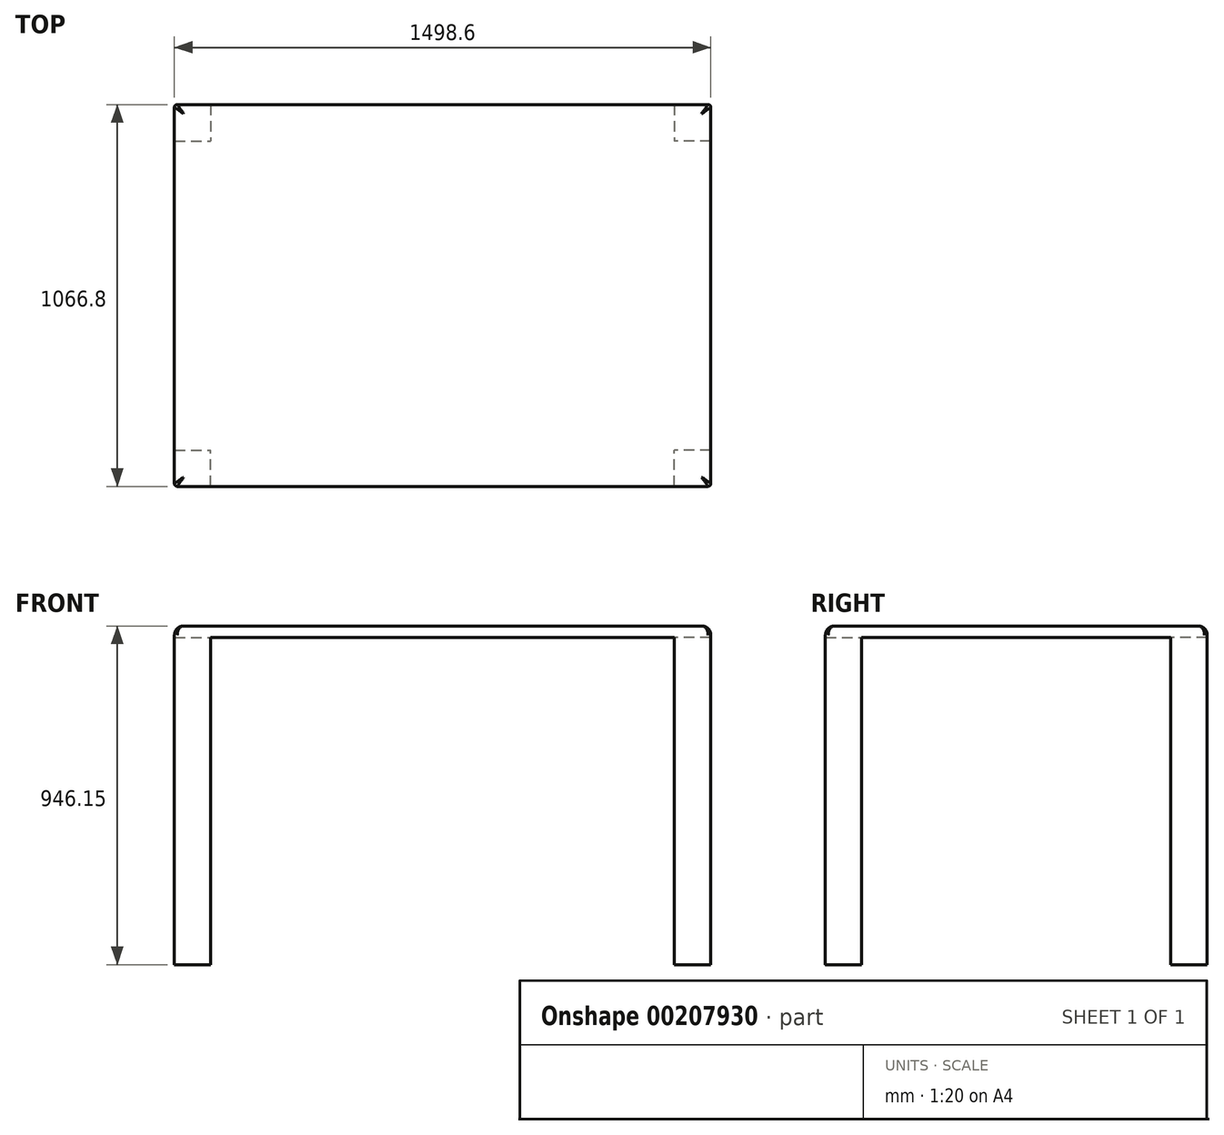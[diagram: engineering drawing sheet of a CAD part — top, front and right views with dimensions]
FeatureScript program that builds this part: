
annotation { "Feature Type Name" : "Feature", "Feature Type Description" : "" }
export const myFeature = defineFeature(function(context is Context, id is Id, definition is map)
    precondition{}
    {
        {
            var Q0;
            Q0=qCreatedBy(makeId("Top.planeOp"),FACE);
            var sketch = newSketch(context, id + "F0", { "sketchPlane" : qUnion([Q0])});
            skLineSegment(sketch, "E0.bottom", {"start": v(-749.3, 533.4) * mm, "end": v(749.3, 533.4) * mm});
            skLineSegment(sketch, "E0.top", {"start": v(-749.3, -533.4) * mm, "end": v(749.3, -533.4) * mm});
            skLineSegment(sketch, "E0.left", {"start": v(-749.3, 533.4) * mm, "end": v(-749.3, -533.4) * mm});
            skLineSegment(sketch, "E0.right", {"start": v(749.3, 533.4) * mm, "end": v(749.3, -533.4) * mm});
            skSolve(sketch);
        }
        {
            var Q0;
            Q0=makeQuery(id+"F0.imprint","IMPRINT",FACE,{"disambiguationData":[TD([[makeQuery(id+"F0.imprint","IMPRINT",EDGE,{"derivedFrom":sQuery(id+"F0.wireOp",EDGE,"E0.bottom")}),-1.0]])]});
            extrude(context, id + "F1", {"entities" : qUnion([Q0]), "depth" : 31.75 * mm});
        }
        {
            var Q0;
            Q0=makeQuery(id+"F1.opExtrude","CAP_EDGE",EDGE,{"disambiguationData":[OSD([sQuery(id+"F0.wireOp",EDGE,"E0.bottom")])],"isStart":false});
            var Q1;
            Q1=makeQuery(id+"F1.opExtrude","CAP_EDGE",EDGE,{"disambiguationData":[OSD([sQuery(id+"F0.wireOp",EDGE,"E0.left")])],"isStart":false});
            var Q2;
            Q2=makeQuery(id+"F1.opExtrude","CAP_EDGE",EDGE,{"disambiguationData":[OSD([sQuery(id+"F0.wireOp",EDGE,"E0.top")])],"isStart":false});
            var Q3;
            Q3=makeQuery(id+"F1.opExtrude","CAP_EDGE",EDGE,{"disambiguationData":[OSD([sQuery(id+"F0.wireOp",EDGE,"E0.right")])],"isStart":false});
            fillet(context, id + "F2", {"entities" : qUnion([Q0, Q1, Q2, Q3]), "radius" : 25.4 * mm, "tangentPropagation" : true, "allowEdgeOverflow" : false});
        }
        {
            var Q0;
            Q0=makeQuery(id+"F1.opExtrude","CAP_FACE",FACE,{"disambiguationData":[OSD([sQuery(id+"F0.wireOp",EDGE,"E0.bottom"),sQuery(id+"F0.wireOp",EDGE,"E0.top"),sQuery(id+"F0.wireOp",EDGE,"E0.left"),sQuery(id+"F0.wireOp",EDGE,"E0.right")])],"isStart":true});
            var sketch = newSketch(context, id + "F3", { "sketchPlane" : qUnion([Q0])});
            skLineSegment(sketch, "E1.bottom", {"start": v(-749.3, 533.4) * mm, "end": v(-647.7, 533.4) * mm});
            skLineSegment(sketch, "E1.top", {"start": v(-749.3, 431.8) * mm, "end": v(-647.7, 431.8) * mm});
            skLineSegment(sketch, "E1.left", {"start": v(-749.3, 533.4) * mm, "end": v(-749.3, 431.8) * mm});
            skLineSegment(sketch, "E1.right", {"start": v(-647.7, 533.4) * mm, "end": v(-647.7, 431.8) * mm});
            skLineSegment(sketch, "E2.bottom", {"start": v(749.3, 533.4) * mm, "end": v(647.7, 533.4) * mm});
            skLineSegment(sketch, "E2.top", {"start": v(749.3, 431.8) * mm, "end": v(647.7, 431.8) * mm});
            skLineSegment(sketch, "E2.left", {"start": v(749.3, 533.4) * mm, "end": v(749.3, 431.8) * mm});
            skLineSegment(sketch, "E2.right", {"start": v(647.7, 533.4) * mm, "end": v(647.7, 431.8) * mm});
            skLineSegment(sketch, "E3.bottom", {"start": v(-749.3, -533.4) * mm, "end": v(-647.7, -533.4) * mm});
            skLineSegment(sketch, "E3.top", {"start": v(-749.3, -431.8) * mm, "end": v(-647.7, -431.8) * mm});
            skLineSegment(sketch, "E3.left", {"start": v(-749.3, -533.4) * mm, "end": v(-749.3, -431.8) * mm});
            skLineSegment(sketch, "E3.right", {"start": v(-647.7, -533.4) * mm, "end": v(-647.7, -431.8) * mm});
            skLineSegment(sketch, "E4.bottom", {"start": v(749.3, -533.4) * mm, "end": v(647.7, -533.4) * mm});
            skLineSegment(sketch, "E4.top", {"start": v(749.3, -431.8) * mm, "end": v(647.7, -431.8) * mm});
            skLineSegment(sketch, "E4.left", {"start": v(749.3, -533.4) * mm, "end": v(749.3, -431.8) * mm});
            skLineSegment(sketch, "E4.right", {"start": v(647.7, -533.4) * mm, "end": v(647.7, -431.8) * mm});
            skSolve(sketch);
        }
        {
            var Q0;
            Q0=makeQuery(id+"F3.imprint","IMPRINT",FACE,{"disambiguationData":[TD([[makeQuery(id+"F3.imprint","IMPRINT",EDGE,{"derivedFrom":sQuery(id+"F3.wireOp",EDGE,"E2.bottom")}),-1.0]])]});
            var Q1;
            Q1=makeQuery(id+"F3.imprint","IMPRINT",FACE,{"disambiguationData":[TD([[makeQuery(id+"F3.imprint","IMPRINT",EDGE,{"derivedFrom":sQuery(id+"F3.wireOp",EDGE,"E3.bottom")}),1.0]])]});
            var Q2;
            Q2=makeQuery(id+"F3.imprint","IMPRINT",FACE,{"disambiguationData":[TD([[makeQuery(id+"F3.imprint","IMPRINT",EDGE,{"derivedFrom":sQuery(id+"F3.wireOp",EDGE,"E4.bottom")}),1.0]])]});
            var Q3;
            Q3=makeQuery(id+"F3.imprint","IMPRINT",FACE,{"disambiguationData":[TD([[makeQuery(id+"F3.imprint","IMPRINT",EDGE,{"derivedFrom":sQuery(id+"F3.wireOp",EDGE,"E1.bottom")}),-1.0]])]});
            extrude(context, id + "F4", {"entities" : qUnion([Q0, Q1, Q2, Q3]), "operationType" : NewBodyOperationType.ADD, "depth" : 914.4 * mm});
        }
        {
            var Q0;
            Q0=makeQuery(id+"F4.boolean.opBoolean","MERGE",EDGE,{"derivedFrom":[makeQuery(id+"F1.opExtrude","SWEPT_EDGE",EDGE,{"disambiguationData":[OSD([sQuery(id+"F0.wireOp",EDGE,"E0.bottom"),sQuery(id+"F0.wireOp",EDGE,"E0.left")])]}),makeQuery(id+"F4.opExtrude","SWEPT_EDGE",EDGE,{"disambiguationData":[OSD([sQuery(id+"F3.wireOp",EDGE,"E3.bottom"),sQuery(id+"F3.wireOp",EDGE,"E3.left")])]})]});
            var Q1;
            Q1=makeQuery(id+"F4.boolean.opBoolean","MERGE",EDGE,{"derivedFrom":[makeQuery(id+"F1.opExtrude","SWEPT_EDGE",EDGE,{"disambiguationData":[OSD([sQuery(id+"F0.wireOp",EDGE,"E0.bottom"),sQuery(id+"F0.wireOp",EDGE,"E0.right")])]}),makeQuery(id+"F4.opExtrude","SWEPT_EDGE",EDGE,{"disambiguationData":[OSD([sQuery(id+"F3.wireOp",EDGE,"E4.bottom"),sQuery(id+"F3.wireOp",EDGE,"E4.left")])]})]});
            var Q2;
            Q2=makeQuery(id+"F4.boolean.opBoolean","MERGE",EDGE,{"derivedFrom":[makeQuery(id+"F1.opExtrude","SWEPT_EDGE",EDGE,{"disambiguationData":[OSD([sQuery(id+"F0.wireOp",EDGE,"E0.top"),sQuery(id+"F0.wireOp",EDGE,"E0.left")])]}),makeQuery(id+"F4.opExtrude","SWEPT_EDGE",EDGE,{"disambiguationData":[OSD([sQuery(id+"F3.wireOp",EDGE,"E1.bottom"),sQuery(id+"F3.wireOp",EDGE,"E1.left")])]})]});
            var Q3;
            Q3=makeQuery(id+"F4.boolean.opBoolean","MERGE",EDGE,{"derivedFrom":[makeQuery(id+"F1.opExtrude","SWEPT_EDGE",EDGE,{"disambiguationData":[OSD([sQuery(id+"F0.wireOp",EDGE,"E0.top"),sQuery(id+"F0.wireOp",EDGE,"E0.right")])]}),makeQuery(id+"F4.opExtrude","SWEPT_EDGE",EDGE,{"disambiguationData":[OSD([sQuery(id+"F3.wireOp",EDGE,"E2.bottom"),sQuery(id+"F3.wireOp",EDGE,"E2.left")])]})]});
            fillet(context, id + "F5", {"entities" : qUnion([Q0, Q1, Q2, Q3]), "radius" : 7.62 * mm, "tangentPropagation" : true, "allowEdgeOverflow" : false});
        }
    });
